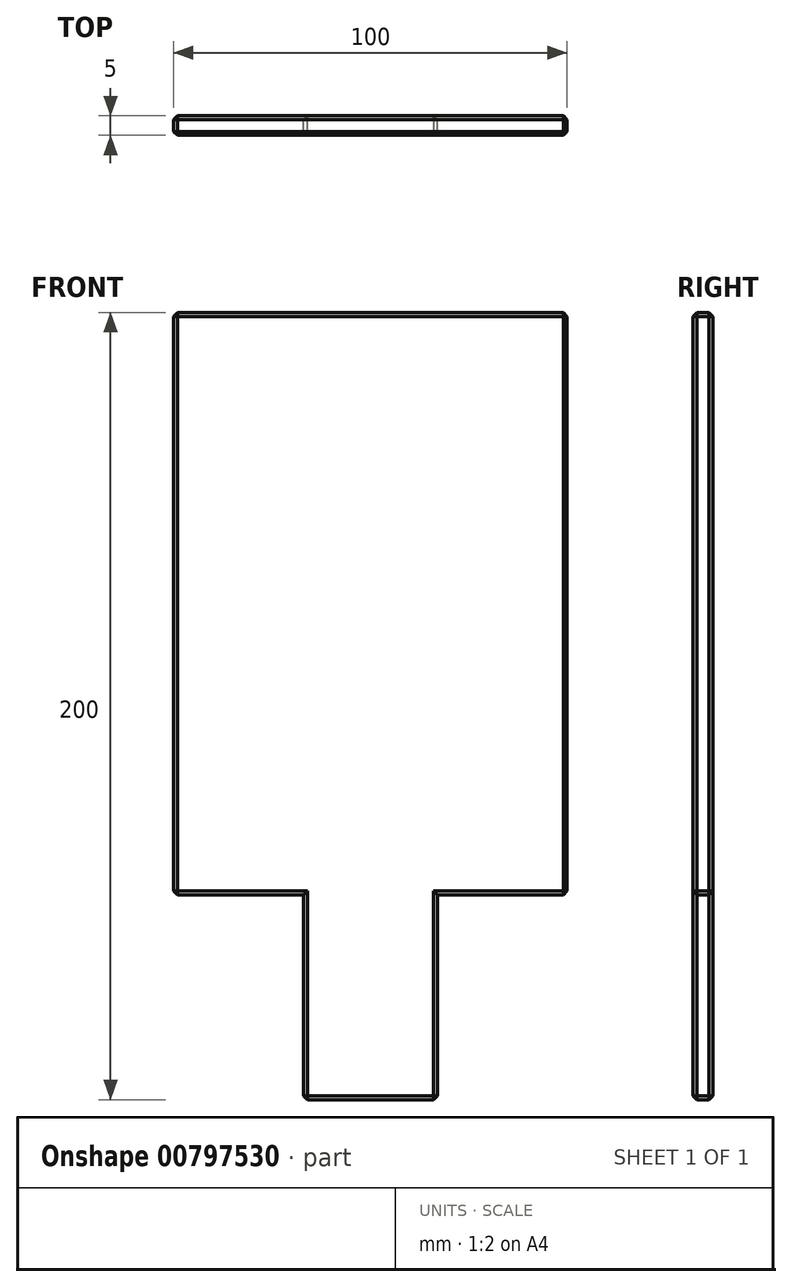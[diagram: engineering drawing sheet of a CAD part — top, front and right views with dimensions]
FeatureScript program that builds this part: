
annotation { "Feature Type Name" : "Feature", "Feature Type Description" : "" }
export const myFeature = defineFeature(function(context is Context, id is Id, definition is map)
    precondition{}
    {
        {
            var Q0;
            Q0=qCreatedBy(makeId("Front.planeOp"),FACE);
            var sketch = newSketch(context, id + "F0", { "sketchPlane" : qUnion([Q0])});
            skLineSegment(sketch, "E0.bottom", {"start": v(13.97, -71.9) * mm, "end": v(-20.03, -71.9) * mm});
            skLineSegment(sketch, "E0.top", {"start": v(46.97, 128.1) * mm, "end": v(-53.03, 128.1) * mm});
            skLineSegment(sketch, "E0.left", {"start": v(46.97, -19.9) * mm, "end": v(46.97, 128.1) * mm});
            skLineSegment(sketch, "E0.right", {"start": v(-53.03, -19.9) * mm, "end": v(-53.03, 128.1) * mm});
            skLineSegment(sketch, "E1", {"start": v(-53.03, -19.9) * mm, "end": v(-20.03, -19.9) * mm});
            skLineSegment(sketch, "E2", {"start": v(-20.03, -19.9) * mm, "end": v(-20.03, -71.9) * mm});
            skLineSegment(sketch, "E3", {"start": v(-3.03, 128.1) * mm, "end": v(-3.03, -71.9) * mm, "construction": true});
            skPoint(sketch, "E4.orphan", {"position": v(-53.03, -71.9) * mm});
            skLineSegment(sketch, "E5.MirrorCS", {"start": v(46.97, -19.9) * mm, "end": v(13.97, -19.9) * mm});
            skLineSegment(sketch, "E6.MirrorCS", {"start": v(13.97, -19.9) * mm, "end": v(13.97, -71.9) * mm});
            skPoint(sketch, "E7.orphan", {"position": v(46.97, -71.9) * mm});
            skSolve(sketch);
        }
        {
            var Q0;
            Q0 = qSketchRegion(id + "F0", true);
            extrude(context, id + "F1", {"entities" : qUnion([Q0]), "depth" : 5 * mm, "offsetDistance" : 25 * mm});
        }
        {
            var Q0;
            Q0=makeQuery(id+"F1.opExtrude","SWEPT_EDGE",EDGE,{"disambiguationData":[OSD([sQuery(id+"F0.wireOp",EDGE,"E0.top"),sQuery(id+"F0.wireOp",EDGE,"E0.right")])]});
            var Q1;
            Q1=makeQuery(id+"F1.opExtrude","CAP_EDGE",EDGE,{"disambiguationData":[OSD([sQuery(id+"F0.wireOp",EDGE,"E0.top")])],"isStart":false});
            var Q2;
            Q2=makeQuery(id+"F1.opExtrude","CAP_FACE",FACE,{"disambiguationData":[OSD([sQuery(id+"F0.wireOp",EDGE,"E0.bottom"),sQuery(id+"F0.wireOp",EDGE,"E0.top"),sQuery(id+"F0.wireOp",EDGE,"E0.left"),sQuery(id+"F0.wireOp",EDGE,"E0.right"),sQuery(id+"F0.wireOp",EDGE,"E1"),sQuery(id+"F0.wireOp",EDGE,"E2"),sQuery(id+"F0.wireOp",EDGE,"E5.MirrorCS"),sQuery(id+"F0.wireOp",EDGE,"E6.MirrorCS")])],"isStart":false});
            var Q3;
            Q3=makeQuery(id+"F1.opExtrude","CAP_EDGE",EDGE,{"disambiguationData":[OSD([sQuery(id+"F0.wireOp",EDGE,"E0.top")])],"isStart":true});
            var Q4;
            Q4=makeQuery(id+"F1.opExtrude","CAP_EDGE",EDGE,{"disambiguationData":[OSD([sQuery(id+"F0.wireOp",EDGE,"E0.right")])],"isStart":true});
            var Q5;
            Q5=makeQuery(id+"F1.opExtrude","CAP_EDGE",EDGE,{"disambiguationData":[OSD([sQuery(id+"F0.wireOp",EDGE,"E0.left")])],"isStart":true});
            var Q6;
            Q6=makeQuery(id+"F1.opExtrude","CAP_EDGE",EDGE,{"disambiguationData":[OSD([sQuery(id+"F0.wireOp",EDGE,"E5.MirrorCS")])],"isStart":true});
            var Q7;
            Q7=makeQuery(id+"F1.opExtrude","CAP_FACE",FACE,{"disambiguationData":[OSD([sQuery(id+"F0.wireOp",EDGE,"E0.bottom"),sQuery(id+"F0.wireOp",EDGE,"E0.top"),sQuery(id+"F0.wireOp",EDGE,"E0.left"),sQuery(id+"F0.wireOp",EDGE,"E0.right"),sQuery(id+"F0.wireOp",EDGE,"E1"),sQuery(id+"F0.wireOp",EDGE,"E2"),sQuery(id+"F0.wireOp",EDGE,"E5.MirrorCS"),sQuery(id+"F0.wireOp",EDGE,"E6.MirrorCS")])],"isStart":true});
            var Q8;
            Q8=makeQuery(id+"F1.opExtrude","SWEPT_EDGE",EDGE,{"disambiguationData":[OSD([sQuery(id+"F0.wireOp",EDGE,"E0.left"),sQuery(id+"F0.wireOp",EDGE,"E5.MirrorCS")])]});
            var Q9;
            Q9=makeQuery(id+"F1.opExtrude","SWEPT_EDGE",EDGE,{"disambiguationData":[OSD([sQuery(id+"F0.wireOp",EDGE,"E0.bottom"),sQuery(id+"F0.wireOp",EDGE,"E6.MirrorCS")])]});
            var Q10;
            Q10=makeQuery(id+"F1.opExtrude","SWEPT_EDGE",EDGE,{"disambiguationData":[OSD([sQuery(id+"F0.wireOp",EDGE,"E0.bottom"),sQuery(id+"F0.wireOp",EDGE,"E2")])]});
            var Q11;
            Q11=makeQuery(id+"F1.opExtrude","SWEPT_EDGE",EDGE,{"disambiguationData":[OSD([sQuery(id+"F0.wireOp",EDGE,"E0.right"),sQuery(id+"F0.wireOp",EDGE,"E1")])]});
            var Q12;
            Q12=makeQuery(id+"F1.opExtrude","SWEPT_EDGE",EDGE,{"disambiguationData":[OSD([sQuery(id+"F0.wireOp",EDGE,"E0.top"),sQuery(id+"F0.wireOp",EDGE,"E0.left")])]});
            chamfer(context, id + "F2", {"entities" : qUnion([Q0, Q1, Q2, Q3, Q4, Q5, Q6, Q7, Q8, Q9, Q10, Q11, Q12]), "width" : 1 * mm, "tangentPropagation" : true});
        }
    });
